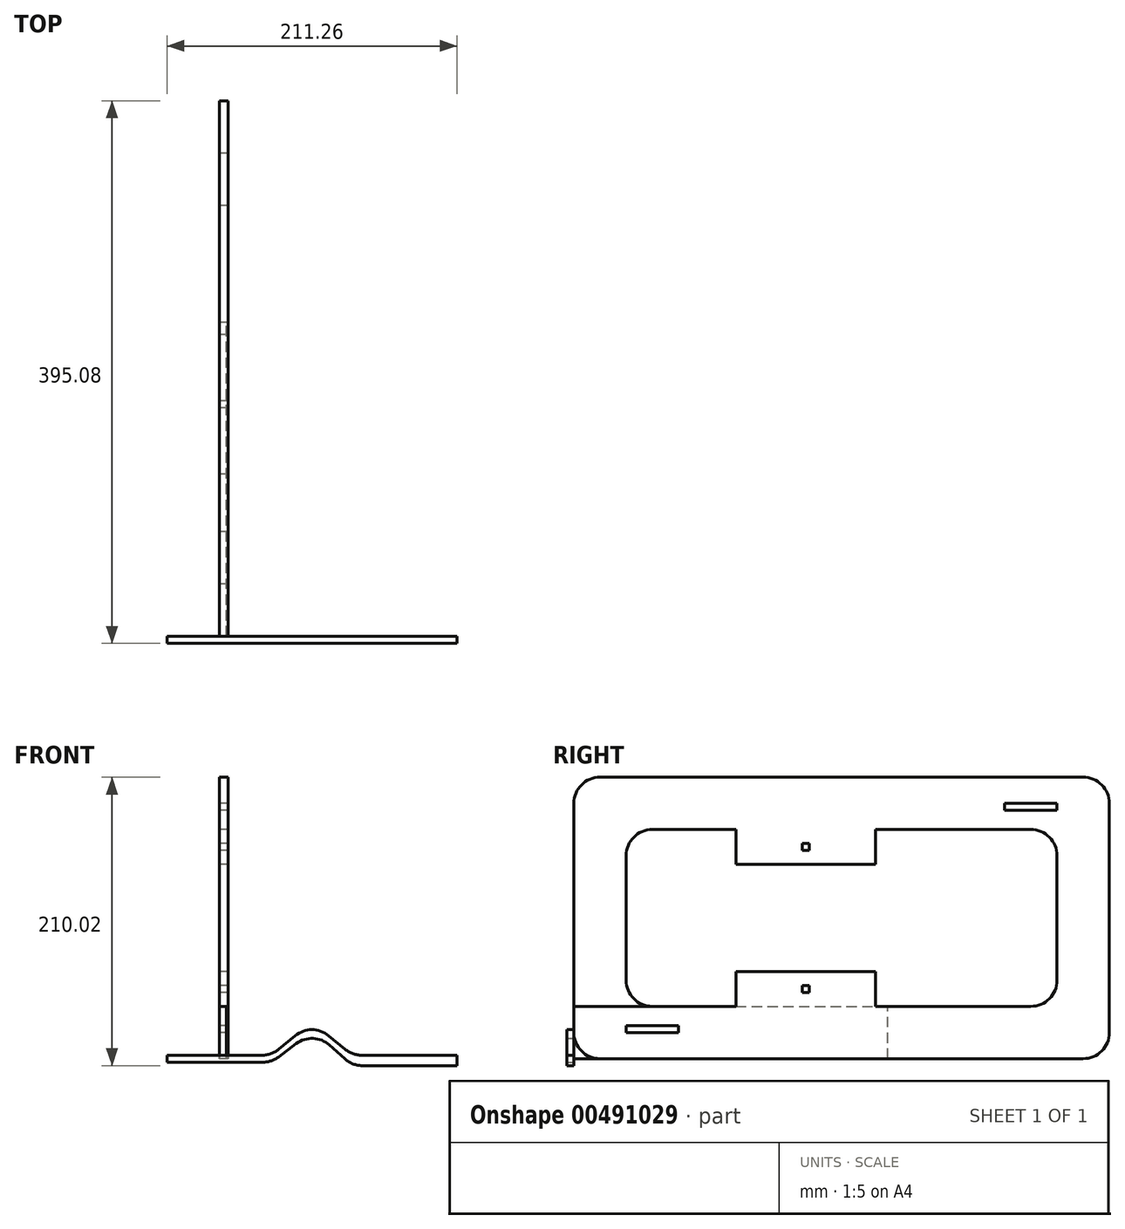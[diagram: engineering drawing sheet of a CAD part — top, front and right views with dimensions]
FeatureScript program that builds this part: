
annotation { "Feature Type Name" : "Feature", "Feature Type Description" : "" }
export const myFeature = defineFeature(function(context is Context, id is Id, definition is map)
    precondition{}
    {
        {
            var Q0;
            Q0=qCreatedBy(makeId("Right.planeOp"),FACE);
            var sketch = newSketch(context, id + "F0", { "sketchPlane" : qUnion([Q0])});
            skLineSegment(sketch, "E0.bottom", {"start": v(19.05, 0) * mm, "end": v(370.95, 0) * mm});
            skLineSegment(sketch, "E0.top", {"start": v(19.05, 205) * mm, "end": v(370.95, 205) * mm});
            skLineSegment(sketch, "E0.left", {"start": v(0, 19.05) * mm, "end": v(0, 185.95) * mm});
            skLineSegment(sketch, "E0.right", {"start": v(390, 19.05) * mm, "end": v(390, 185.95) * mm});
            skPoint(sketch, "E1.visualSharp", {"position": v(0, 205) * mm});
            skLineSegment(sketch, "E1.filletArc", {"start": v(0, 205) * mm, "end": v(0, 205) * mm});
            skPoint(sketch, "E2.visualSharp", {"position": v(0, 0) * mm});
            skLineSegment(sketch, "E2.filletArc", {"start": v(0, 0) * mm, "end": v(0, 0) * mm});
            skPoint(sketch, "E3.visualSharp", {"position": v(390, 0) * mm});
            skLineSegment(sketch, "E3.filletArc", {"start": v(390, 0) * mm, "end": v(390, 0) * mm});
            skPoint(sketch, "E4.visualSharp", {"position": v(390, 205) * mm});
            skLineSegment(sketch, "E4.filletArc", {"start": v(390, 205) * mm, "end": v(390, 205) * mm});
            skLineSegment(sketch, "E5.0", {"start": v(57.15, 166.9) * mm, "end": v(118.08, 166.9) * mm});
            skLineSegment(sketch, "E5.1", {"start": v(38.1, 57.15) * mm, "end": v(38.1, 147.85) * mm});
            skLineSegment(sketch, "E5.2", {"start": v(57.15, 38.1) * mm, "end": v(118.08, 38.1) * mm});
            skLineSegment(sketch, "E5.3", {"start": v(351.9, 57.15) * mm, "end": v(351.9, 147.85) * mm});
            skArc(sketch, "E6.filletArc", {"start": v(19.05, 205) * mm, "mid": v(5.58, 199.42) * mm, "end": v(0, 185.95) * mm});
            skArc(sketch, "E7.filletArc", {"start": v(390, 185.95) * mm, "mid": v(384.42, 199.42) * mm, "end": v(370.95, 205) * mm});
            skArc(sketch, "E8.filletArc", {"start": v(370.95, 0) * mm, "mid": v(384.42, 5.58) * mm, "end": v(390, 19.05) * mm});
            skArc(sketch, "E9.filletArc", {"start": v(0, 19.05) * mm, "mid": v(5.58, 5.58) * mm, "end": v(19.05, 0) * mm});
            skPoint(sketch, "E10.visualSharp", {"position": v(38.1, 166.9) * mm});
            skArc(sketch, "E10.filletArc", {"start": v(57.15, 166.9) * mm, "mid": v(43.68, 161.32) * mm, "end": v(38.1, 147.85) * mm});
            skPoint(sketch, "E11.visualSharp", {"position": v(351.9, 166.9) * mm});
            skPoint(sketch, "E12.visualSharp", {"position": v(351.9, 38.1) * mm});
            skArc(sketch, "E12.filletArc", {"start": v(332.85, 38.1) * mm, "mid": v(346.32, 43.68) * mm, "end": v(351.9, 57.15) * mm});
            skPoint(sketch, "E13.visualSharp", {"position": v(38.1, 38.1) * mm});
            skLineSegment(sketch, "E14", {"start": v(176.58, 166.9) * mm, "end": v(176.58, 166.9) * mm});
            skLineSegment(sketch, "E15", {"start": v(219.68, 166.9) * mm, "end": v(332.85, 166.9) * mm});
            skLineSegment(sketch, "E16", {"start": v(38.1, 38.1) * mm, "end": v(38.1, 38.1) * mm});
            skArc(sketch, "E17.filletArc", {"start": v(38.1, 57.15) * mm, "mid": v(43.68, 43.68) * mm, "end": v(57.15, 38.1) * mm});
            skArc(sketch, "E18.filletArc", {"start": v(351.9, 147.85) * mm, "mid": v(346.32, 161.32) * mm, "end": v(332.85, 166.9) * mm});
            skLineSegment(sketch, "E19", {"start": v(118.08, 38.1) * mm, "end": v(118.08, 63.5) * mm});
            skLineSegment(sketch, "E20", {"start": v(118.08, 63.5) * mm, "end": v(219.68, 63.5) * mm});
            skLineSegment(sketch, "E21", {"start": v(219.68, 63.5) * mm, "end": v(219.68, 38.1) * mm});
            skLineSegment(sketch, "E22", {"start": v(118.08, 166.9) * mm, "end": v(118.08, 141.5) * mm});
            skLineSegment(sketch, "E23", {"start": v(118.08, 141.5) * mm, "end": v(219.68, 141.5) * mm});
            skLineSegment(sketch, "E24", {"start": v(219.68, 141.5) * mm, "end": v(219.68, 166.9) * mm});
            skLineSegment(sketch, "E25.trimOffspring", {"start": v(219.68, 38.1) * mm, "end": v(332.85, 38.1) * mm});
            skLineSegment(sketch, "E26.bottom", {"start": v(38.1, 24.13) * mm, "end": v(76.2, 24.13) * mm});
            skLineSegment(sketch, "E26.top", {"start": v(38.1, 19.05) * mm, "end": v(76.2, 19.05) * mm});
            skLineSegment(sketch, "E26.left", {"start": v(38.1, 24.13) * mm, "end": v(38.1, 19.05) * mm});
            skLineSegment(sketch, "E26.right", {"start": v(76.2, 24.13) * mm, "end": v(76.2, 19.05) * mm});
            skLineSegment(sketch, "E27.bottom", {"start": v(313.8, 185.95) * mm, "end": v(351.9, 185.95) * mm});
            skLineSegment(sketch, "E27.top", {"start": v(313.8, 180.87) * mm, "end": v(351.9, 180.87) * mm});
            skLineSegment(sketch, "E27.left", {"start": v(313.8, 185.95) * mm, "end": v(313.8, 180.87) * mm});
            skLineSegment(sketch, "E27.right", {"start": v(351.9, 185.95) * mm, "end": v(351.9, 180.87) * mm});
            skLineSegment(sketch, "E28", {"start": v(195, 0) * mm, "end": v(195, 107.33) * mm, "construction": true});
            skLineSegment(sketch, "E29.bottom", {"start": v(171.42, 48.26) * mm, "end": v(166.34, 48.26) * mm});
            skLineSegment(sketch, "E29.top", {"start": v(171.42, 53.34) * mm, "end": v(166.34, 53.34) * mm});
            skLineSegment(sketch, "E29.left", {"start": v(171.42, 48.26) * mm, "end": v(171.42, 53.34) * mm});
            skLineSegment(sketch, "E29.right", {"start": v(166.34, 48.26) * mm, "end": v(166.34, 53.34) * mm});
            skPoint(sketch, "E29.middle", {"position": v(168.88, 50.8) * mm});
            skPoint(sketch, "E29.middle.positionSnap0", {"position": v(168.88, 63.5) * mm});
            skPoint(sketch, "E29.middle.positionSnap1", {"position": v(118.08, 50.8) * mm});
            skPoint(sketch, "E29.centerSnap0", {"position": v(168.88, 63.5) * mm});
            skPoint(sketch, "E29.centerSnap1", {"position": v(118.08, 50.8) * mm});
            skLineSegment(sketch, "E30.bottom", {"start": v(171.42, 156.74) * mm, "end": v(166.34, 156.74) * mm});
            skLineSegment(sketch, "E30.top", {"start": v(171.42, 151.66) * mm, "end": v(166.34, 151.66) * mm});
            skLineSegment(sketch, "E30.left", {"start": v(171.42, 156.74) * mm, "end": v(171.42, 151.66) * mm});
            skLineSegment(sketch, "E30.right", {"start": v(166.34, 156.74) * mm, "end": v(166.34, 151.66) * mm});
            skPoint(sketch, "E30.middle", {"position": v(168.88, 154.2) * mm});
            skPoint(sketch, "E30.middle.positionSnap0", {"position": v(168.88, 141.5) * mm});
            skPoint(sketch, "E30.middle.positionSnap1", {"position": v(118.08, 154.2) * mm});
            skPoint(sketch, "E30.centerSnap0", {"position": v(168.88, 141.5) * mm});
            skPoint(sketch, "E30.centerSnap1", {"position": v(118.08, 154.2) * mm});
            skSolve(sketch);
        }
        {
            var Q0;
            Q0=makeQuery(id+"F0.imprint","IMPRINT",FACE,{"disambiguationData":[TD([[makeQuery(id+"F0.imprint","IMPRINT",EDGE,{"derivedFrom":sQuery(id+"F0.wireOp",EDGE,"E0.bottom")}),1.0]])]});
            extrude(context, id + "F1", {"entities" : qUnion([Q0]), "depth" : 6.35 * mm});
        }
        {
            var Q0;
            Q0=qCreatedBy(makeId("Right.planeOp"),FACE);
            var sketch = newSketch(context, id + "F2", { "sketchPlane" : qUnion([Q0])});
            skLineSegment(sketch, "E31.bottom", {"start": v(0, 0) * mm, "end": v(228.6, 0) * mm});
            skLineSegment(sketch, "E31.top", {"start": v(0, 38.1) * mm, "end": v(228.6, 38.1) * mm});
            skLineSegment(sketch, "E31.left", {"start": v(0, 0) * mm, "end": v(0, 38.1) * mm});
            skLineSegment(sketch, "E31.right", {"start": v(228.6, 0) * mm, "end": v(228.6, 38.1) * mm});
            skSolve(sketch);
        }
        {
            var Q0;
            Q0=makeQuery(id+"F2.imprint","IMPRINT",FACE,{"disambiguationData":[TD([[makeQuery(id+"F2.imprint","IMPRINT",EDGE,{"derivedFrom":sQuery(id+"F2.wireOp",EDGE,"E31.bottom")}),1.0]])]});
            extrude(context, id + "F3", {"entities" : qUnion([Q0]), "depth" : 5.08 * mm});
        }
        {
            var Q0;
            Q0=qCreatedBy(makeId("Front.planeOp"),FACE);
            var sketch = newSketch(context, id + "F4", { "sketchPlane" : qUnion([Q0])});
            skLineSegment(sketch, "E32.bottom", {"start": v(-38.1, 2.54) * mm, "end": v(31.27, 2.54) * mm});
            skLineSegment(sketch, "E32.top", {"start": v(-38.1, -2.54) * mm, "end": v(31.74, -2.54) * mm});
            skLineSegment(sketch, "E32.left", {"start": v(-38.1, 2.54) * mm, "end": v(-38.1, -2.54) * mm});
            skPoint(sketch, "E32.middle", {"position": v(0, 0) * mm});
            skLineSegment(sketch, "E33", {"start": v(43.37, 6.87) * mm, "end": v(55.43, 16.79) * mm});
            skLineSegment(sketch, "E34", {"start": v(79.63, 16.79) * mm, "end": v(91.69, 6.87) * mm});
            skLineSegment(sketch, "E35", {"start": v(103.79, 2.54) * mm, "end": v(173.16, 2.54) * mm});
            skLineSegment(sketch, "E36", {"start": v(173.16, 2.54) * mm, "end": v(173.16, -5.02) * mm});
            skLineSegment(sketch, "E37", {"start": v(173.16, -5.02) * mm, "end": v(104.23, -5.02) * mm});
            skLineSegment(sketch, "E38", {"start": v(91.54, -0.18) * mm, "end": v(80.2, 9.95) * mm});
            skLineSegment(sketch, "E39", {"start": v(56.06, 10.97) * mm, "end": v(43.19, 1.29) * mm});
            skPoint(sketch, "E40.visualSharp", {"position": v(38.1, 2.54) * mm});
            skArc(sketch, "E40.filletArc", {"start": v(31.27, 2.54) * mm, "mid": v(37.7, 3.66) * mm, "end": v(43.37, 6.87) * mm});
            skPoint(sketch, "E41.visualSharp", {"position": v(38.1, -2.54) * mm});
            skArc(sketch, "E41.filletArc", {"start": v(31.74, -2.54) * mm, "mid": v(37.77, -1.56) * mm, "end": v(43.19, 1.29) * mm});
            skPoint(sketch, "E42.visualSharp", {"position": v(67.53, 26.74) * mm});
            skArc(sketch, "E42.filletArc", {"start": v(79.63, 16.79) * mm, "mid": v(67.53, 21.12) * mm, "end": v(55.43, 16.79) * mm});
            skPoint(sketch, "E43.visualSharp", {"position": v(68.55, 20.36) * mm});
            skArc(sketch, "E43.filletArc", {"start": v(80.2, 9.95) * mm, "mid": v(68.31, 14.78) * mm, "end": v(56.06, 10.97) * mm});
            skPoint(sketch, "E44.visualSharp", {"position": v(96.96, 2.54) * mm});
            skArc(sketch, "E44.filletArc", {"start": v(91.69, 6.87) * mm, "mid": v(97.36, 3.66) * mm, "end": v(103.79, 2.54) * mm});
            skPoint(sketch, "E45.visualSharp", {"position": v(96.96, -5.02) * mm});
            skArc(sketch, "E45.filletArc", {"start": v(91.54, -0.18) * mm, "mid": v(97.44, -3.77) * mm, "end": v(104.23, -5.02) * mm});
            skSolve(sketch);
        }
        {
            var Q0;
            Q0 = qSketchRegion(id + "F4", true);
            extrude(context, id + "F5", {"entities" : qUnion([Q0]), "depth" : 5.08 * mm});
        }
    });
